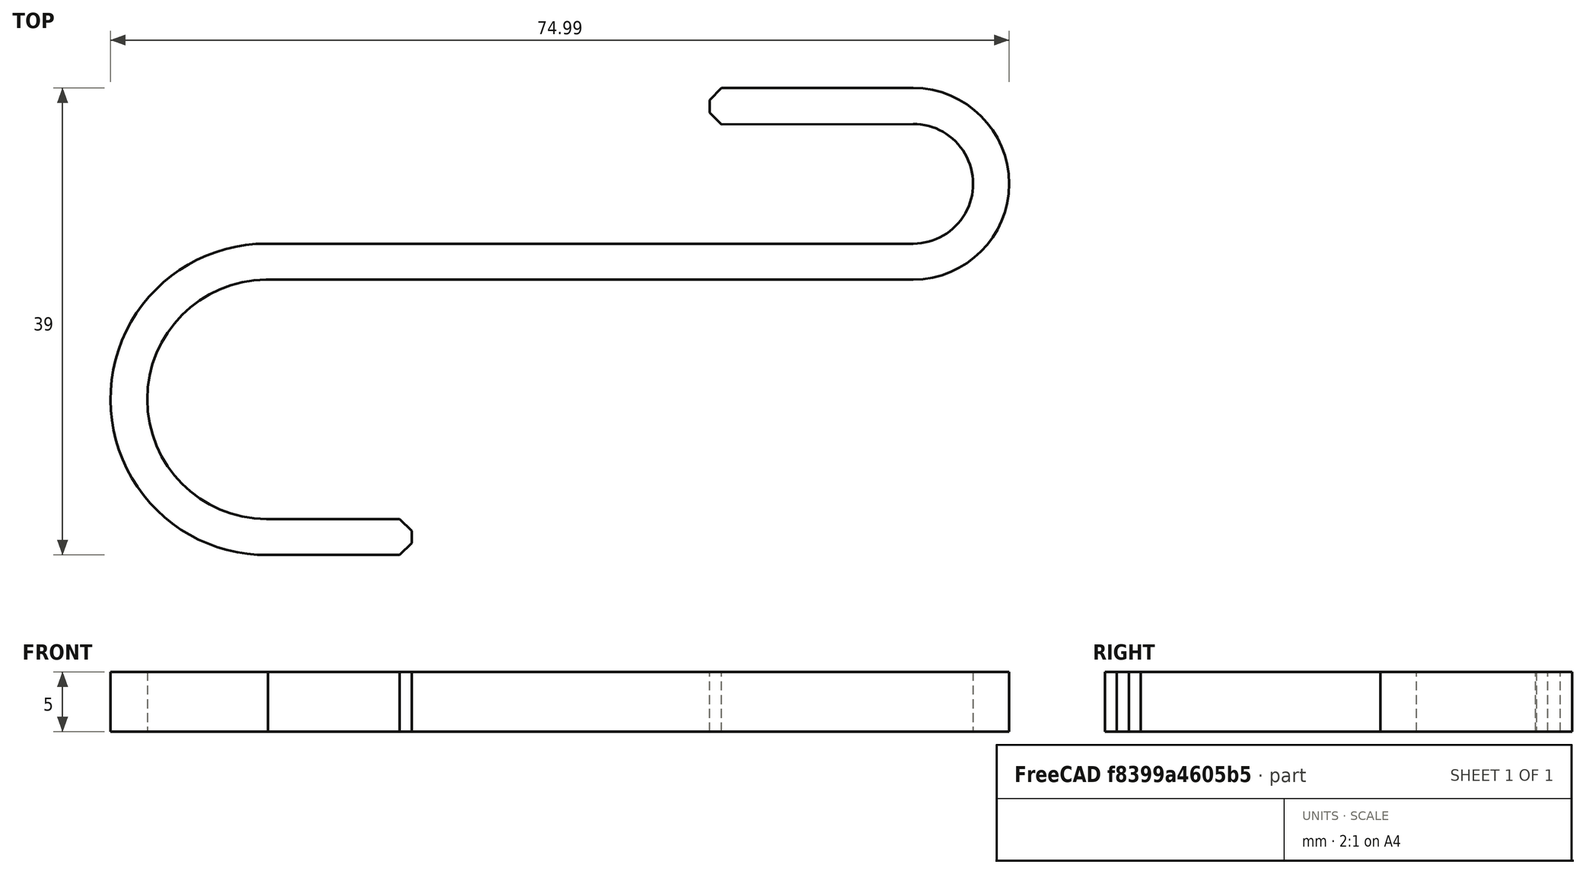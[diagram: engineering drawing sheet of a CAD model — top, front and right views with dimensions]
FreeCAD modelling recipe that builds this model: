
FCSTD DOCUMENT  (FreeCAD 0.14R3702 (Git))
Label: gancho_seve3
License: CC-BY 3.0
LicenseURL: http://creativecommons.org/licenses/by/3.0/
objects: Sketcher::SketchObject×1, PartDesign::Pad×1, Part::Chamfer×1, App::MeasureDistance×1
note: 4 computed .brp shape members not serialized (recipe doc carries the construction recipe); baked Part::Feature solids carry a one-line shape summary decoded from their .brp

FEATURE [Sketcher::SketchObject] Sketch
  sketch-geometry (14):
    g0: LineSegment StartX=-27.0041 StartY=1.5 StartZ=0 EndX=27.0041 EndY=1.5 EndZ=0
    g1: GeomPoint [constr] X=-26.9362 Y=-11.5 Z=0
    g2: GeomPoint [constr] X=-26.9968 Y=-21.5001 Z=0
    g3: ArcOfCircle CenterX=-26.9362 CenterY=-11.5 CenterZ=0 NormalX=0 NormalY=0 NormalZ=1 Radius=10.0003 StartAngle=1.5788 EndAngle=4.70633
    g4: ArcOfCircle CenterX=-27.0041 CenterY=-11.5004 CenterZ=0 NormalX=0 NormalY=0 NormalZ=1 Radius=13.0004 StartAngle=1.5708 EndAngle=4.72283
    g5: LineSegment StartX=-26.9968 StartY=-21.5001 StartZ=0 EndX=-14.8683 EndY=-21.5001 EndZ=0
    g6: LineSegment StartX=-14.8683 StartY=-21.5001 StartZ=0 EndX=-14.8683 EndY=-24.5 EndZ=0
    g7: LineSegment StartX=-14.8683 StartY=-24.5 StartZ=0 EndX=-26.8683 EndY=-24.5 EndZ=0
    g8: ArcOfCircle CenterX=26.9898 CenterY=6.5 CenterZ=0 NormalX=0 NormalY=0 NormalZ=1 Radius=5.00002 StartAngle=4.71526 EndAngle=7.85685
    g9: LineSegment StartX=-27.0163 StartY=-1.5 StartZ=0 EndX=27.0041 EndY=-1.5 EndZ=0
    g10: ArcOfCircle CenterX=26.9898 CenterY=6.5 CenterZ=0 NormalX=0 NormalY=0 NormalZ=1 Radius=8.00001 StartAngle=4.71418 EndAngle=7.85265
    g11: LineSegment StartX=26.9754 StartY=11.5 StartZ=0 EndX=10.0005 EndY=11.4513 EndZ=0
    g12: LineSegment StartX=10.0005 StartY=11.4513 StartZ=0 EndX=10.0005 EndY=14.5 EndZ=0
    g13: LineSegment StartX=10.0005 StartY=14.5 StartZ=0 EndX=27.0005 EndY=14.5 EndZ=0
  constraints (30):
    c: Symmetric(g0,g0,g-2)
    c: Coincident(g3,g2)
    c: Coincident(g4,g0)
    c: Symmetric(g0,g4,g1)
    c: Coincident(g5,g2)
    c: Horizontal(g5)
    c: Coincident(g5,g6)
    c: Vertical(g6)
    c: Coincident(g6,g7)
    c: Coincident(g7,g4)
    c: Horizontal(g7)
    c: Distance(g4,g6) = 12
    c: DistanceY(g0,g8) = 5
    c: Symmetric(g0,g8,g8)
    c: Horizontal(g9)
    c: Coincident(g10,g8)
    c: Coincident(g10,g9)
    c: Symmetric(g9,g0,g-1)
    c: Tangent(g8,g11)
    c: Coincident(g11,g12)
    c: Vertical(g12)
    c: Coincident(g12,g13)
    c: Coincident(g13,g10)
    c: Horizontal(g13)
    c: DistanceX(g12,g10) = 17
    c: Coincident(g3,g9)
    c: DistanceY(g0,g3) = -3
    c: Coincident(g8,g0)
    c: DistanceY(g3,g1) = -10
    c: Coincident(g1,g3)
FEATURE [PartDesign::Pad] Pad
  Length = 5
  Length2 = 100
  Sketch = -> Sketch
  Type = 0
FEATURE [Part::Chamfer] Chamfer
  Base = -> Pad
  Edges = 4 edges r=1: [Edge5,Edge8,Edge23,Edge26]
FEATURE [App::MeasureDistance] Distance  label="Distance: 20.347"
  Distance = 20.3468
  P1 = (-27.0148,-1.5,5)
  P2 = (-27.4228,-21.8427,5)
